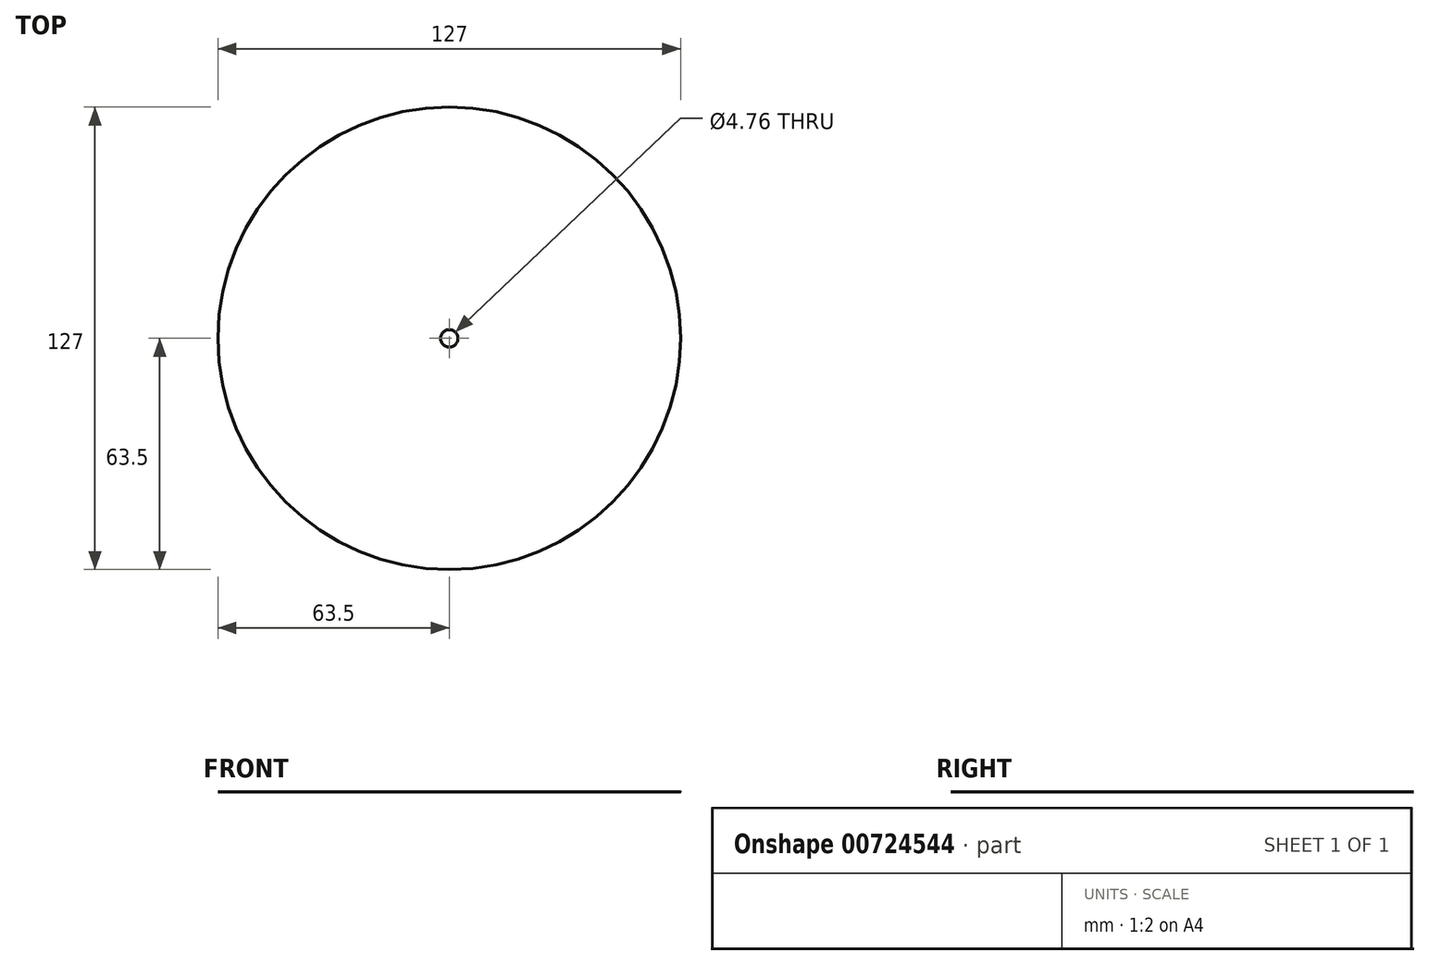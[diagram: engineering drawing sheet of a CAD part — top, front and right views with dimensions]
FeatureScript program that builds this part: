
annotation { "Feature Type Name" : "Feature", "Feature Type Description" : "" }
export const myFeature = defineFeature(function(context is Context, id is Id, definition is map)
    precondition{}
    {
        {
            var Q0;
            Q0=qCreatedBy(makeId("Top.planeOp"),FACE);
            var sketch = newSketch(context, id + "F0", { "sketchPlane" : qUnion([Q0])});
            skCircle(sketch, "E0", {"center": v(0, 0) * mm, "radius": 63.5 * mm});
            skCircle(sketch, "E1", {"center": v(0, 0) * mm, "radius": 2.38 * mm});
            skSolve(sketch);
        }
        {
            var Q0;
            Q0 = qSketchRegion(id + "F0", true);
            extrude(context, id + "F1", {"entities" : qUnion([Q0]), "depth" : 1 / 203.2 * mm, "offsetDistance" : 25.4 * mm});
        }
    });
